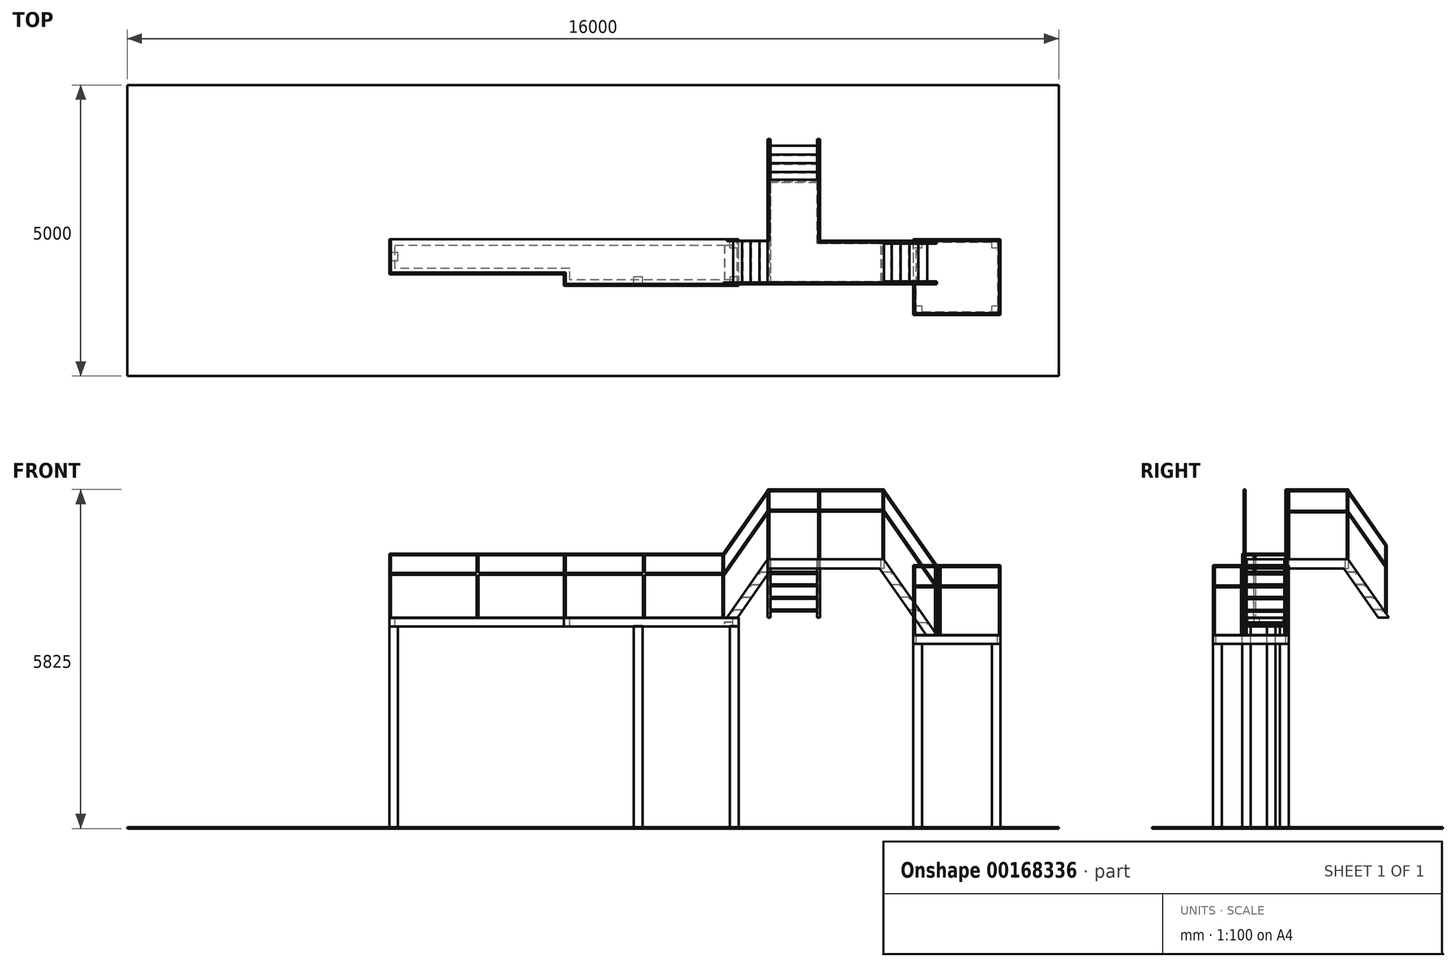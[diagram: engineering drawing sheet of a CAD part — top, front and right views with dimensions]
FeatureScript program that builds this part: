
annotation { "Feature Type Name" : "Feature", "Feature Type Description" : "" }
export const myFeature = defineFeature(function(context is Context, id is Id, definition is map)
    precondition{}
    {
        {
            var Q0;
            Q0=qCreatedBy(makeId("Top.planeOp"),FACE);
            var sketch = newSketch(context, id + "F0", { "sketchPlane" : qUnion([Q0])});
            skLineSegment(sketch, "E0.bottom", {"start": v(-500, 1500) * mm, "end": v(15500, 1500) * mm});
            skLineSegment(sketch, "E0.top", {"start": v(-500, -3500) * mm, "end": v(15500, -3500) * mm});
            skLineSegment(sketch, "E0.left", {"start": v(-500, 1500) * mm, "end": v(-500, -3500) * mm});
            skLineSegment(sketch, "E0.right", {"start": v(15500, 1500) * mm, "end": v(15500, -3500) * mm});
            skSolve(sketch);
        }
        {
            var Q0;
            Q0 = qSketchRegion(id + "F0", true);
            extrude(context, id + "F1", {"entities" : qUnion([Q0]), "oppositeDirection" : true, "depth" : 25 * mm});
        }
        {
            var Q0;
            Q0=qCreatedBy(makeId("Top.planeOp"),FACE);
            cPlane(context, id + "F2", {"entities" : qUnion([Q0]), "cplaneType" : CPlaneType.OFFSET, "offset" : 3600 * mm, "width" : 150 * mm, "height" : 150 * mm});
        }
        {
            var Q0;
            Q0=qCreatedBy(id+"F2.planeOp",FACE);
            var sketch = newSketch(context, id + "F3", { "sketchPlane" : qUnion([Q0])});
            skLineSegment(sketch, "E1", {"start": v(4000, -1150) * mm, "end": v(10000, -1150) * mm});
            skLineSegment(sketch, "E2", {"start": v(10000, -1950) * mm, "end": v(10000, -1150) * mm});
            skLineSegment(sketch, "E3", {"start": v(10000, -1950) * mm, "end": v(7000, -1950) * mm});
            skLineSegment(sketch, "E4", {"start": v(7000, -1950) * mm, "end": v(7000, -1750) * mm});
            skLineSegment(sketch, "E5", {"start": v(7000, -1750) * mm, "end": v(4000, -1750) * mm});
            skLineSegment(sketch, "E6", {"start": v(4000, -1750) * mm, "end": v(4000, -1150) * mm});
            skSolve(sketch);
        }
        {
            var Q0;
            Q0 = qSketchRegion(id + "F3", true);
            extrude(context, id + "F4", {"entities" : qUnion([Q0]), "oppositeDirection" : true, "depth" : 5 * mm});
        }
        {
            var Q0;
            Q0=makeQuery(id+"F4.opExtrude","SWEPT_FACE",FACE,{"disambiguationData":[OSD([sQuery(id+"F3.wireOp",EDGE,"E2")])]});
            var sketch = newSketch(context, id + "F5", { "sketchPlane" : qUnion([Q0])});
            skLineSegment(sketch, "E7.bottom", {"start": v(-1950, 3595) * mm, "end": v(-1850, 3595) * mm});
            skLineSegment(sketch, "E7.top", {"start": v(-1950, 3445) * mm, "end": v(-1850, 3445) * mm});
            skLineSegment(sketch, "E7.left", {"start": v(-1950, 3595) * mm, "end": v(-1950, 3445) * mm});
            skLineSegment(sketch, "E7.right", {"start": v(-1850, 3595) * mm, "end": v(-1850, 3445) * mm});
            skSolve(sketch);
        }
        {
            var Q0;
            Q0=qCreatedBy(id+"F2.planeOp",FACE);
            cPlane(context, id + "F6", {"entities" : qUnion([Q0]), "cplaneType" : CPlaneType.OFFSET, "offset" : 150 * mm, "oppositeDirection" : true, "width" : 150 * mm, "height" : 150 * mm});
        }
        {
            var Q0;
            Q0=qCreatedBy(id+"F6.planeOp",FACE);
            var sketch = newSketch(context, id + "F7", { "sketchPlane" : qUnion([Q0])});
            skLineSegment(sketch, "E8.0", {"start": v(10000, -1150) * mm, "end": v(10000, -1950) * mm});
            skLineSegment(sketch, "E9.0", {"start": v(10000, -1950) * mm, "end": v(7000, -1950) * mm});
            skLineSegment(sketch, "E10.0", {"start": v(7000, -1750) * mm, "end": v(4000, -1750) * mm});
            skLineSegment(sketch, "E11.0", {"start": v(7000, -1950) * mm, "end": v(7000, -1750) * mm});
            skLineSegment(sketch, "E12.0", {"start": v(4000, -1750) * mm, "end": v(4000, -1150) * mm});
            skLineSegment(sketch, "E13.0", {"start": v(4000, -1150) * mm, "end": v(10000, -1150) * mm});
            skPoint(sketch, "E14.0", {"position": v(10000, -1150) * mm});
            skSolve(sketch);
        }
        {
            var Q0;
            Q0=makeQuery(id+"F5.imprint","IMPRINT",FACE,{"disambiguationData":[TD([[makeQuery(id+"F5.imprint","IMPRINT",EDGE,{"derivedFrom":sQuery(id+"F5.wireOp",EDGE,"E7.bottom")}),-1.0]])]});
            var Q1;
            Q1 = qConstructionFilter(qBodyType(qCreatedBy(id + "F7" ,EDGE), BodyType.WIRE), ConstructionObject.NO);
            sweep(context, id + "F8", {"profiles" : qUnion([Q0]), "path" : qUnion([Q1])});
        }
        {
            var Q0;
            Q0=qCreatedBy(id+"F6.planeOp",FACE);
            var sketch = newSketch(context, id + "F9", { "sketchPlane" : qUnion([Q0])});
            skLineSegment(sketch, "E15.bottom", {"start": v(4000, -1375) * mm, "end": v(4150, -1375) * mm});
            skLineSegment(sketch, "E15.top", {"start": v(4000, -1525) * mm, "end": v(4150, -1525) * mm});
            skLineSegment(sketch, "E15.left", {"start": v(4000, -1375) * mm, "end": v(4000, -1525) * mm});
            skLineSegment(sketch, "E15.right", {"start": v(4150, -1375) * mm, "end": v(4150, -1525) * mm});
            skLineSegment(sketch, "E16.bottom", {"start": v(8200, -1800) * mm, "end": v(8350, -1800) * mm});
            skLineSegment(sketch, "E16.top", {"start": v(8200, -1950) * mm, "end": v(8350, -1950) * mm});
            skLineSegment(sketch, "E16.left", {"start": v(8200, -1800) * mm, "end": v(8200, -1950) * mm});
            skLineSegment(sketch, "E16.right", {"start": v(8350, -1800) * mm, "end": v(8350, -1950) * mm});
            skLineSegment(sketch, "E17.bottom", {"start": v(9850, -1150) * mm, "end": v(10000, -1150) * mm});
            skLineSegment(sketch, "E17.top", {"start": v(9850, -1300) * mm, "end": v(10000, -1300) * mm});
            skLineSegment(sketch, "E17.left", {"start": v(9850, -1150) * mm, "end": v(9850, -1300) * mm});
            skLineSegment(sketch, "E17.right", {"start": v(10000, -1150) * mm, "end": v(10000, -1300) * mm});
            skLineSegment(sketch, "E18.bottom", {"start": v(9850, -1950) * mm, "end": v(10000, -1950) * mm});
            skLineSegment(sketch, "E18.top", {"start": v(9850, -1800) * mm, "end": v(10000, -1800) * mm});
            skLineSegment(sketch, "E18.left", {"start": v(9850, -1950) * mm, "end": v(9850, -1800) * mm});
            skLineSegment(sketch, "E18.right", {"start": v(10000, -1950) * mm, "end": v(10000, -1800) * mm});
            skSolve(sketch);
        }
        {
            var Q0;
            Q0 = qSketchRegion(id + "F9", true);
            var Q1;
            Q1=makeQuery(id+"F1.opExtrude","CAP_FACE",FACE,{"disambiguationData":[OSD([sQuery(id+"F0.wireOp",EDGE,"E0.bottom"),sQuery(id+"F0.wireOp",EDGE,"E0.top"),sQuery(id+"F0.wireOp",EDGE,"E0.left"),sQuery(id+"F0.wireOp",EDGE,"E0.right")])],"isStart":true});
            extrude(context, id + "F10", {"entities" : qUnion([Q0]), "endBound" : BoundingType.UP_TO_SURFACE, "oppositeDirection" : true, "endBoundEntityFace" : qUnion([Q1]), "depth" : 25 * mm});
        }
        {
            var Q0;
            Q0=qCreatedBy(id+"F2.planeOp",FACE);
            cPlane(context, id + "F11", {"entities" : qUnion([Q0]), "cplaneType" : CPlaneType.OFFSET, "offset" : 300 * mm, "oppositeDirection" : true, "width" : 150 * mm, "height" : 150 * mm});
        }
        {
            var Q0;
            Q0=qCreatedBy(id+"F11.planeOp",FACE);
            var sketch = newSketch(context, id + "F12", { "sketchPlane" : qUnion([Q0])});
            skLineSegment(sketch, "E19.bottom", {"start": v(13000, -1150) * mm, "end": v(14500, -1150) * mm});
            skLineSegment(sketch, "E19.top", {"start": v(13000, -2450) * mm, "end": v(14500, -2450) * mm});
            skLineSegment(sketch, "E19.left", {"start": v(13000, -1150) * mm, "end": v(13000, -2450) * mm});
            skLineSegment(sketch, "E19.right", {"start": v(14500, -1150) * mm, "end": v(14500, -2450) * mm});
            skPoint(sketch, "E20.0", {"position": v(10000, -1150) * mm});
            skSolve(sketch);
        }
        {
            var Q0;
            Q0 = qSketchRegion(id + "F12", true);
            extrude(context, id + "F13", {"entities" : qUnion([Q0]), "oppositeDirection" : true, "depth" : 5 * mm});
        }
        {
            var Q0;
            Q0=qCreatedBy(id+"F11.planeOp",FACE);
            cPlane(context, id + "F14", {"entities" : qUnion([Q0]), "cplaneType" : CPlaneType.OFFSET, "offset" : 1300 * mm, "width" : 150 * mm, "height" : 150 * mm});
        }
        {
            var Q0;
            Q0=qCreatedBy(id+"F14.planeOp",FACE);
            var sketch = newSketch(context, id + "F15", { "sketchPlane" : qUnion([Q0])});
            skLineSegment(sketch, "E21.bottom", {"start": v(10500, -125) * mm, "end": v(11400, -125) * mm});
            skLineSegment(sketch, "E21.top", {"start": v(10500, -1925) * mm, "end": v(12500, -1925) * mm});
            skLineSegment(sketch, "E21.left", {"start": v(10500, -125) * mm, "end": v(10500, -1925) * mm});
            skLineSegment(sketch, "E21.right", {"start": v(11400, -125) * mm, "end": v(11400, -1175) * mm});
            skLineSegment(sketch, "E22", {"start": v(10950, -1777.45) * mm, "end": v(10950, -125) * mm, "construction": true});
            skLineSegment(sketch, "E23", {"start": v(12500, -1925) * mm, "end": v(12500, -1175) * mm});
            skLineSegment(sketch, "E24", {"start": v(12500, -1175) * mm, "end": v(11400, -1175) * mm});
            skSolve(sketch);
        }
        {
            var Q0;
            Q0 = qSketchRegion(id + "F15", true);
            extrude(context, id + "F16", {"entities" : qUnion([Q0]), "oppositeDirection" : true, "depth" : 5 * mm});
        }
        {
            var Q0;
            Q0=makeQuery(id+"F16.opExtrude","CAP_EDGE",EDGE,{"disambiguationData":[OSD([sQuery(id+"F15.wireOp",EDGE,"E23")])],"isStart":false});
            cPoint(context, id + "F17", {"entities" : qUnion([Q0]), "parameter" : 0.5});
        }
        {
            var Q0;
            Q0=makeQuery(id+"F16.opExtrude","SWEPT_FACE",FACE,{"disambiguationData":[OSD([sQuery(id+"F15.wireOp",EDGE,"E21.top")])]});
            var Q1;
            Q1 = qCreatedBy(id + "F17" ,VERTEX);
            cPlane(context, id + "F18", {"entities" : qUnion([Q0, Q1]), "cplaneType" : CPlaneType.PLANE_POINT, "offset" : 388 * mm, "oppositeDirection" : true, "width" : 150 * mm, "height" : 150 * mm});
        }
        {
            var Q0;
            Q0=qCreatedBy(id+"F18.planeOp",FACE);
            var sketch = newSketch(context, id + "F19", { "sketchPlane" : qUnion([Q0])});
            skLineSegment(sketch, "E25", {"start": v(10500, 4600) * mm, "end": v(10500, 4338.48) * mm});
            skLineSegment(sketch, "E26", {"start": v(10500, 4338.48) * mm, "end": v(9982.9, 3600) * mm});
            skLineSegment(sketch, "E27", {"start": v(9982.9, 3600) * mm, "end": v(9799.8, 3600) * mm});
            skLineSegment(sketch, "E28", {"start": v(9799.8, 3600) * mm, "end": v(10500, 4600) * mm});
            skSolve(sketch);
        }
        {
            var Q0;
            Q0 = qSketchRegion(id + "F19", true);
            extrude(context, id + "F20", {"entities" : qUnion([Q0]), "endBound" : BoundingType.SYMMETRIC, "depth" : 750 * mm});
        }
        {
            var Q0;
            Q0=makeQuery(id+"F20.opExtrude","SWEPT_FACE",FACE,{"disambiguationData":[OSD([sQuery(id+"F19.wireOp",EDGE,"E28")])]});
            var Q1;
            Q1=makeQuery(id+"F20.opExtrude","SWEPT_FACE",FACE,{"disambiguationData":[OSD([sQuery(id+"F19.wireOp",EDGE,"E25")])]});
            var Q2;
            Q2=makeQuery(id+"F20.opExtrude","SWEPT_FACE",FACE,{"disambiguationData":[OSD([sQuery(id+"F19.wireOp",EDGE,"E27")])]});
            shell(context, id + "F21", {"entities" : qUnion([Q0, Q1, Q2]), "thickness" : 3 * mm});
        }
        {
            var Q0;
            Q0=makeQuery(id+"F20.opExtrude","CAP_FACE",FACE,{"disambiguationData":[OSD([sQuery(id+"F19.wireOp",EDGE,"E25"),sQuery(id+"F19.wireOp",EDGE,"E26"),sQuery(id+"F19.wireOp",EDGE,"E27"),sQuery(id+"F19.wireOp",EDGE,"E28")])],"isStart":false});
            var sketch = newSketch(context, id + "F22", { "sketchPlane" : qUnion([Q0])});
            skLineSegment(sketch, "E29", {"start": v(10359.07, 4350) * mm, "end": v(10359.07, 4385) * mm});
            skLineSegment(sketch, "E30", {"start": v(10359.07, 4385) * mm, "end": v(10529.07, 4385) * mm});
            skLineSegment(sketch, "E31.0", {"start": v(10364.07, 4380) * mm, "end": v(10529.07, 4380) * mm});
            skLineSegment(sketch, "E31.1", {"start": v(10364.07, 4350) * mm, "end": v(10364.07, 4380) * mm});
            skLineSegment(sketch, "E32", {"start": v(10359.07, 4350) * mm, "end": v(10364.07, 4350) * mm});
            skLineSegment(sketch, "E33", {"start": v(10529.07, 4385) * mm, "end": v(10529.07, 4380) * mm});
            skLineSegment(sketch, "E34.1.0.0", {"start": v(10213.22, 4134.56) * mm, "end": v(10213.22, 4164.56) * mm});
            skLineSegment(sketch, "E34.1.0.1", {"start": v(10213.22, 4164.56) * mm, "end": v(10378.22, 4164.56) * mm});
            skLineSegment(sketch, "E34.1.0.2", {"start": v(10208.22, 4169.56) * mm, "end": v(10378.22, 4169.56) * mm});
            skLineSegment(sketch, "E34.1.0.3", {"start": v(10208.22, 4134.56) * mm, "end": v(10208.22, 4169.56) * mm});
            skLineSegment(sketch, "E34.1.0.4", {"start": v(10378.22, 4169.56) * mm, "end": v(10378.22, 4164.56) * mm});
            skLineSegment(sketch, "E34.1.0.5", {"start": v(10208.22, 4134.56) * mm, "end": v(10213.22, 4134.56) * mm});
            skLineSegment(sketch, "E34.2.0.0", {"start": v(10062.37, 3919.13) * mm, "end": v(10062.37, 3949.13) * mm});
            skLineSegment(sketch, "E34.2.0.1", {"start": v(10062.37, 3949.13) * mm, "end": v(10227.37, 3949.13) * mm});
            skLineSegment(sketch, "E34.2.0.2", {"start": v(10057.37, 3954.13) * mm, "end": v(10227.37, 3954.13) * mm});
            skLineSegment(sketch, "E34.2.0.3", {"start": v(10057.37, 3919.13) * mm, "end": v(10057.37, 3954.13) * mm});
            skLineSegment(sketch, "E34.2.0.4", {"start": v(10227.37, 3954.13) * mm, "end": v(10227.37, 3949.13) * mm});
            skLineSegment(sketch, "E34.2.0.5", {"start": v(10057.37, 3919.13) * mm, "end": v(10062.37, 3919.13) * mm});
            skLineSegment(sketch, "E34.direction1", {"start": v(10359.07, 4350) * mm, "end": v(10208.22, 4134.56) * mm, "construction": true});
            skLineSegment(sketch, "E35.0.3.0", {"start": v(9911.52, 3703.69) * mm, "end": v(9911.52, 3733.69) * mm});
            skLineSegment(sketch, "E35.3.3.0", {"start": v(9911.52, 3733.69) * mm, "end": v(10076.52, 3733.69) * mm});
            skLineSegment(sketch, "E35.6.3.0", {"start": v(9906.52, 3738.69) * mm, "end": v(10076.52, 3738.69) * mm});
            skLineSegment(sketch, "E35.9.3.0", {"start": v(9906.52, 3703.69) * mm, "end": v(9906.52, 3738.69) * mm});
            skLineSegment(sketch, "E35.12.3.0", {"start": v(10076.52, 3738.69) * mm, "end": v(10076.52, 3733.69) * mm});
            skLineSegment(sketch, "E35.15.3.0", {"start": v(9906.52, 3703.69) * mm, "end": v(9911.52, 3703.69) * mm});
            skLineSegment(sketch, "E35.0.4.0", {"start": v(9760.67, 3488.25) * mm, "end": v(9760.67, 3518.25) * mm});
            skLineSegment(sketch, "E35.3.4.0", {"start": v(9760.67, 3518.25) * mm, "end": v(9925.67, 3518.25) * mm});
            skLineSegment(sketch, "E35.6.4.0", {"start": v(9755.67, 3523.25) * mm, "end": v(9925.67, 3523.25) * mm});
            skLineSegment(sketch, "E35.9.4.0", {"start": v(9755.67, 3488.25) * mm, "end": v(9755.67, 3523.25) * mm});
            skLineSegment(sketch, "E35.12.4.0", {"start": v(9925.67, 3523.25) * mm, "end": v(9925.67, 3518.25) * mm});
            skLineSegment(sketch, "E35.15.4.0", {"start": v(9755.67, 3488.25) * mm, "end": v(9760.67, 3488.25) * mm});
            skSolve(sketch);
        }
        {
            var Q0;
            Q0 = qSketchRegion(id + "F22", true);
            var Q1;
            Q1=makeQuery(id+"F20.opExtrude","CAP_FACE",FACE,{"disambiguationData":[OSD([sQuery(id+"F19.wireOp",EDGE,"E25"),sQuery(id+"F19.wireOp",EDGE,"E26"),sQuery(id+"F19.wireOp",EDGE,"E27"),sQuery(id+"F19.wireOp",EDGE,"E28")])],"isStart":true});
            extrude(context, id + "F23", {"entities" : qUnion([Q0]), "operationType" : NewBodyOperationType.ADD, "endBound" : BoundingType.UP_TO_SURFACE, "oppositeDirection" : true, "endBoundEntityFace" : qUnion([Q1]), "depth" : 25 * mm});
        }
        {
            var Q0;
            Q0=makeQuery(id+"F16.opExtrude","CAP_EDGE",EDGE,{"disambiguationData":[OSD([sQuery(id+"F15.wireOp",EDGE,"E21.bottom")])],"isStart":true});
            cPoint(context, id + "F24", {"entities" : qUnion([Q0]), "parameter" : 0.5});
        }
        {
            var Q0;
            Q0=makeQuery(id+"F16.opExtrude","SWEPT_FACE",FACE,{"disambiguationData":[OSD([sQuery(id+"F15.wireOp",EDGE,"E21.left")])]});
            var Q1;
            Q1 = qCreatedBy(id + "F24" ,VERTEX);
            cPlane(context, id + "F25", {"entities" : qUnion([Q0, Q1]), "cplaneType" : CPlaneType.PLANE_POINT, "offset" : 25 * mm, "width" : 150 * mm, "height" : 150 * mm});
        }
        {
            var Q0;
            Q0=makeQuery(id+"F16.opExtrude","CAP_FACE",FACE,{"disambiguationData":[OSD([sQuery(id+"F15.wireOp",EDGE,"E21.bottom"),sQuery(id+"F15.wireOp",EDGE,"E21.top"),sQuery(id+"F15.wireOp",EDGE,"E21.left"),sQuery(id+"F15.wireOp",EDGE,"E21.right")])],"isStart":false});
            var sketch = newSketch(context, id + "F26", { "sketchPlane" : qUnion([Q0])});
            skLineSegment(sketch, "E36.0.0", {"start": v(10500, 125) * mm, "end": v(11400, 125) * mm});
            skLineSegment(sketch, "E36.0.1", {"start": v(11400, 125) * mm, "end": v(11400, 125) * mm});
            skLineSegment(sketch, "E36.0.2", {"start": v(10530, 1925) * mm, "end": v(10500, 1925) * mm});
            skLineSegment(sketch, "E36.0.3", {"start": v(10500, 1925) * mm, "end": v(10500, 125) * mm});
            skLineSegment(sketch, "E37.0", {"start": v(-505, -1505) * mm, "end": v(15505, -1505) * mm});
            skLineSegment(sketch, "E37.1", {"start": v(-505, 3505) * mm, "end": v(-505, -1505) * mm});
            skLineSegment(sketch, "E37.2", {"start": v(15505, 3505) * mm, "end": v(-505, 3505) * mm});
            skLineSegment(sketch, "E37.3", {"start": v(15505, -1505) * mm, "end": v(15505, 3505) * mm});
            skLineSegment(sketch, "E38.0", {"start": v(11350, 1225) * mm, "end": v(11350, 175) * mm});
            skLineSegment(sketch, "E38.1", {"start": v(10550, 175) * mm, "end": v(10550, 1875) * mm});
            skLineSegment(sketch, "E38.2", {"start": v(10550, 1875) * mm, "end": v(12450, 1875) * mm});
            skLineSegment(sketch, "E38.3", {"start": v(11350, 175) * mm, "end": v(10550, 175) * mm});
            skLineSegment(sketch, "E38.4", {"start": v(12450, 1875) * mm, "end": v(12450, 1225) * mm});
            skLineSegment(sketch, "E38.5", {"start": v(12450, 1225) * mm, "end": v(11350, 1225) * mm});
            skSolve(sketch);
        }
        {
            var Q0;
            Q0=makeQuery(id+"F26.imprint","IMPRINT",FACE,{"disambiguationData":[TD([[makeQuery(id+"F26.imprint","IMPRINT",EDGE,{"derivedFrom":sQuery(id+"F26.wireOp",EDGE,"E36.0.0")}),1.0]])]});
            extrude(context, id + "F27", {"entities" : qUnion([Q0]), "depth" : 150 * mm});
        }
        {
            var Q0;
            Q0=makeQuery(id+"F27.opExtrude","SWEPT_FACE",FACE,{"disambiguationData":[OSD([sQuery(id+"F15.wireOp",EDGE,"E21.right")])]});
            var sketch = newSketch(context, id + "F28", { "sketchPlane" : qUnion([Q0])});
            skLineSegment(sketch, "E39", {"start": v(-125, 4595) * mm, "end": v(-203.09, 4445) * mm});
            skLineSegment(sketch, "E40", {"start": v(387.9, 3601) * mm, "end": v(-203.09, 4445) * mm});
            skLineSegment(sketch, "E41", {"start": v(-125, 4595) * mm, "end": v(571, 3601) * mm});
            skLineSegment(sketch, "E42", {"start": v(571, 3601) * mm, "end": v(387.9, 3601) * mm});
            skSolve(sketch);
        }
        {
            var Q0;
            Q0 = qSketchRegion(id + "F28", true);
            extrude(context, id + "F29", {"entities" : qUnion([Q0]), "oppositeDirection" : true, "depth" : 50 * mm});
        }
        {
            var Q0;
            Q0=makeQuery(id+"F29.opExtrude","SWEPT_BODY",BODY,{"disambiguationData":[OSD([sQuery(id+"F28.wireOp",EDGE,"E39"),sQuery(id+"F28.wireOp",EDGE,"E40"),sQuery(id+"F28.wireOp",EDGE,"yFBp22pC-zta5-zhW2-1WAF-goKuTXkOEWaN"),sQuery(id+"F28.wireOp",EDGE,"E41")])]});
            var Q1;
            Q1=qCreatedBy(id+"F25.planeOp",FACE);
            mirror(context, id + "F30", {"operationType" : NewBodyOperationType.ADD, "entities" : qUnion([Q0]), "mirrorPlane" : qUnion([Q1])});
        }
        {
            var Q0;
            Q0=makeQuery(id+"F30.boolean.opBoolean","MERGE",FACE,{"derivedFrom":[makeQuery(id+"F27.opExtrude","SWEPT_FACE",FACE,{"disambiguationData":[OSD([sQuery(id+"F26.wireOp",EDGE,"4b7b3fe2-faf2-46bd-95d1-659c540ad528.3")])]}),makeQuery(id+"F29.opExtrude","CAP_FACE",FACE,{"disambiguationData":[OSD([sQuery(id+"F28.wireOp",EDGE,"E39"),sQuery(id+"F28.wireOp",EDGE,"E40"),sQuery(id+"F28.wireOp",EDGE,"yFBp22pC-zta5-zhW2-1WAF-goKuTXkOEWaN"),sQuery(id+"F28.wireOp",EDGE,"E41")])],"isStart":false})]});
            var sketch = newSketch(context, id + "F31", { "sketchPlane" : qUnion([Q0])});
            skLineSegment(sketch, "E43", {"start": v(-7.43, 4385) * mm, "end": v(157.57, 4385) * mm});
            skLineSegment(sketch, "E44", {"start": v(157.57, 4385) * mm, "end": v(157.57, 4380) * mm});
            skLineSegment(sketch, "E45", {"start": v(157.57, 4380) * mm, "end": v(-2.43, 4380) * mm});
            skLineSegment(sketch, "E46", {"start": v(-2.43, 4380) * mm, "end": v(-2.43, 4350) * mm});
            skLineSegment(sketch, "E47", {"start": v(-2.43, 4350) * mm, "end": v(-7.43, 4350) * mm});
            skLineSegment(sketch, "E48", {"start": v(-7.43, 4350) * mm, "end": v(-7.43, 4385) * mm});
            skLineSegment(sketch, "E49.1.0.0", {"start": v(-157.7, 4170.38) * mm, "end": v(7.3, 4170.38) * mm});
            skLineSegment(sketch, "E49.1.0.1", {"start": v(7.3, 4165.38) * mm, "end": v(-152.7, 4165.38) * mm});
            skLineSegment(sketch, "E49.1.0.2", {"start": v(-152.7, 4135.38) * mm, "end": v(-157.7, 4135.38) * mm});
            skLineSegment(sketch, "E49.1.0.3", {"start": v(-157.7, 4135.38) * mm, "end": v(-157.7, 4170.38) * mm});
            skLineSegment(sketch, "E49.1.0.4", {"start": v(-152.7, 4165.38) * mm, "end": v(-152.7, 4135.38) * mm});
            skLineSegment(sketch, "E49.1.0.5", {"start": v(7.3, 4170.38) * mm, "end": v(7.3, 4165.38) * mm});
            skLineSegment(sketch, "E49.2.0.0", {"start": v(-307.98, 3955.76) * mm, "end": v(-142.98, 3955.76) * mm});
            skLineSegment(sketch, "E49.2.0.1", {"start": v(-142.98, 3950.76) * mm, "end": v(-302.98, 3950.76) * mm});
            skLineSegment(sketch, "E49.2.0.2", {"start": v(-302.98, 3920.76) * mm, "end": v(-307.98, 3920.76) * mm});
            skLineSegment(sketch, "E49.2.0.3", {"start": v(-307.98, 3920.76) * mm, "end": v(-307.98, 3955.76) * mm});
            skLineSegment(sketch, "E49.2.0.4", {"start": v(-302.98, 3950.76) * mm, "end": v(-302.98, 3920.76) * mm});
            skLineSegment(sketch, "E49.2.0.5", {"start": v(-142.98, 3955.76) * mm, "end": v(-142.98, 3950.76) * mm});
            skLineSegment(sketch, "E49.direction1", {"start": v(-7.43, 4350) * mm, "end": v(-157.7, 4135.38) * mm, "construction": true});
            skLineSegment(sketch, "E50.0.3.0", {"start": v(-458.26, 3741.15) * mm, "end": v(-293.26, 3741.15) * mm});
            skLineSegment(sketch, "E50.3.3.0", {"start": v(-293.26, 3736.15) * mm, "end": v(-453.26, 3736.15) * mm});
            skLineSegment(sketch, "E50.6.3.0", {"start": v(-453.26, 3706.15) * mm, "end": v(-458.26, 3706.15) * mm});
            skLineSegment(sketch, "E50.9.3.0", {"start": v(-458.26, 3706.15) * mm, "end": v(-458.26, 3741.15) * mm});
            skLineSegment(sketch, "E50.12.3.0", {"start": v(-453.26, 3736.15) * mm, "end": v(-453.26, 3706.15) * mm});
            skLineSegment(sketch, "E50.15.3.0", {"start": v(-293.26, 3741.15) * mm, "end": v(-293.26, 3736.15) * mm});
            skSolve(sketch);
        }
        {
            var Q0;
            Q0 = qSketchRegion(id + "F31", true);
            var Q1;
            Q1=makeQuery(id+"F30.boolean.opBoolean","MERGE",FACE,{"derivedFrom":[makeQuery(id+"F27.opExtrude","SWEPT_FACE",FACE,{"disambiguationData":[OSD([sQuery(id+"F26.wireOp",EDGE,"E38.1")])]}),makeQuery(id+"F30.opPattern","COPY",FACE,{"derivedFrom":makeQuery(id+"F29.opExtrude","CAP_FACE",FACE,{"disambiguationData":[OSD([sQuery(id+"F28.wireOp",EDGE,"E39"),sQuery(id+"F28.wireOp",EDGE,"E40"),sQuery(id+"F28.wireOp",EDGE,"E41"),sQuery(id+"F28.wireOp",EDGE,"E42")])],"isStart":false}),"instanceName":"1"})]});
            extrude(context, id + "F32", {"entities" : qUnion([Q0]), "operationType" : NewBodyOperationType.ADD, "endBound" : BoundingType.UP_TO_SURFACE, "endBoundEntityFace" : qUnion([Q1]), "depth" : 413 * mm});
        }
        {
            var Q0;
            Q0=qCreatedBy(id+"F18.planeOp",FACE);
            var sketch = newSketch(context, id + "F33", { "sketchPlane" : qUnion([Q0])});
            skLineSegment(sketch, "E51", {"start": v(12500, 4595) * mm, "end": v(12421.91, 4445) * mm});
            skLineSegment(sketch, "E52", {"start": v(12421.91, 4445) * mm, "end": v(13223.65, 3300) * mm});
            skLineSegment(sketch, "E53", {"start": v(13223.65, 3300) * mm, "end": v(13406.77, 3300) * mm});
            skLineSegment(sketch, "E54", {"start": v(13406.77, 3300) * mm, "end": v(12500, 4595) * mm});
            skSolve(sketch);
        }
        {
            var Q0;
            Q0 = qSketchRegion(id + "F33", true);
            extrude(context, id + "F34", {"entities" : qUnion([Q0]), "depth" : 375 * mm, "hasSecondDirection" : true, "secondDirectionOppositeDirection" : false, "secondDirectionDepth" : 325 * mm});
        }
        {
            var Q0;
            Q0=makeQuery(id+"F34.opExtrude","SWEPT_BODY",BODY,{"disambiguationData":[OSD([sQuery(id+"F33.wireOp",EDGE,"E51"),sQuery(id+"F33.wireOp",EDGE,"E52"),sQuery(id+"F33.wireOp",EDGE,"E53"),sQuery(id+"F33.wireOp",EDGE,"E54")])]});
            var Q1;
            Q1=qCreatedBy(id+"F18.planeOp",FACE);
            mirror(context, id + "F35", {"operationType" : NewBodyOperationType.ADD, "entities" : qUnion([Q0]), "mirrorPlane" : qUnion([Q1])});
        }
        {
            var Q0;
            Q0=qCreatedBy(id+"F18.planeOp",FACE);
            var sketch = newSketch(context, id + "F36", { "sketchPlane" : qUnion([Q0])});
            skLineSegment(sketch, "E55", {"start": v(12467.43, 4385) * mm, "end": v(12632.43, 4385) * mm});
            skLineSegment(sketch, "E56", {"start": v(12467.43, 4385) * mm, "end": v(12467.43, 4380) * mm});
            skLineSegment(sketch, "E57", {"start": v(12627.43, 4380) * mm, "end": v(12467.43, 4380) * mm});
            skLineSegment(sketch, "E58", {"start": v(12627.43, 4380) * mm, "end": v(12627.43, 4350) * mm});
            skLineSegment(sketch, "E59", {"start": v(12632.43, 4350) * mm, "end": v(12627.43, 4350) * mm});
            skLineSegment(sketch, "E60", {"start": v(12632.43, 4350) * mm, "end": v(12632.43, 4385) * mm});
            skLineSegment(sketch, "E61.1.0.0", {"start": v(12784.43, 4132.92) * mm, "end": v(12784.43, 4167.92) * mm});
            skLineSegment(sketch, "E61.1.0.1", {"start": v(12619.43, 4167.92) * mm, "end": v(12784.43, 4167.92) * mm});
            skLineSegment(sketch, "E61.1.0.2", {"start": v(12779.43, 4162.92) * mm, "end": v(12619.43, 4162.92) * mm});
            skLineSegment(sketch, "E61.1.0.3", {"start": v(12779.43, 4162.92) * mm, "end": v(12779.43, 4132.92) * mm});
            skLineSegment(sketch, "E61.1.0.4", {"start": v(12784.43, 4132.92) * mm, "end": v(12779.43, 4132.92) * mm});
            skLineSegment(sketch, "E61.1.0.5", {"start": v(12619.43, 4167.92) * mm, "end": v(12619.43, 4162.92) * mm});
            skLineSegment(sketch, "E61.2.0.0", {"start": v(12936.42, 3915.85) * mm, "end": v(12936.42, 3950.85) * mm});
            skLineSegment(sketch, "E61.2.0.1", {"start": v(12771.42, 3950.85) * mm, "end": v(12936.42, 3950.85) * mm});
            skLineSegment(sketch, "E61.2.0.2", {"start": v(12931.42, 3945.85) * mm, "end": v(12771.42, 3945.85) * mm});
            skLineSegment(sketch, "E61.2.0.3", {"start": v(12931.42, 3945.85) * mm, "end": v(12931.42, 3915.85) * mm});
            skLineSegment(sketch, "E61.2.0.4", {"start": v(12936.42, 3915.85) * mm, "end": v(12931.42, 3915.85) * mm});
            skLineSegment(sketch, "E61.2.0.5", {"start": v(12771.42, 3950.85) * mm, "end": v(12771.42, 3945.85) * mm});
            skLineSegment(sketch, "E61.direction1", {"start": v(12467.43, 4380) * mm, "end": v(12619.43, 4162.92) * mm, "construction": true});
            skLineSegment(sketch, "E62.0.3.0", {"start": v(13088.42, 3698.77) * mm, "end": v(13088.42, 3733.77) * mm});
            skLineSegment(sketch, "E62.3.3.0", {"start": v(12923.42, 3733.77) * mm, "end": v(13088.42, 3733.77) * mm});
            skLineSegment(sketch, "E62.6.3.0", {"start": v(13083.42, 3728.77) * mm, "end": v(12923.42, 3728.77) * mm});
            skLineSegment(sketch, "E62.9.3.0", {"start": v(13083.42, 3728.77) * mm, "end": v(13083.42, 3698.77) * mm});
            skLineSegment(sketch, "E62.12.3.0", {"start": v(13088.42, 3698.77) * mm, "end": v(13083.42, 3698.77) * mm});
            skLineSegment(sketch, "E62.15.3.0", {"start": v(12923.42, 3733.77) * mm, "end": v(12923.42, 3728.77) * mm});
            skLineSegment(sketch, "E62.0.4.0", {"start": v(13240.42, 3481.7) * mm, "end": v(13240.42, 3516.7) * mm});
            skLineSegment(sketch, "E62.3.4.0", {"start": v(13075.42, 3516.7) * mm, "end": v(13240.42, 3516.7) * mm});
            skLineSegment(sketch, "E62.6.4.0", {"start": v(13235.42, 3511.7) * mm, "end": v(13075.42, 3511.7) * mm});
            skLineSegment(sketch, "E62.9.4.0", {"start": v(13235.42, 3511.7) * mm, "end": v(13235.42, 3481.7) * mm});
            skLineSegment(sketch, "E62.12.4.0", {"start": v(13240.42, 3481.7) * mm, "end": v(13235.42, 3481.7) * mm});
            skLineSegment(sketch, "E62.15.4.0", {"start": v(13075.42, 3516.7) * mm, "end": v(13075.42, 3511.7) * mm});
            skSolve(sketch);
        }
        {
            var Q0;
            Q0 = qSketchRegion(id + "F36", true);
            extrude(context, id + "F37", {"entities" : qUnion([Q0]), "operationType" : NewBodyOperationType.ADD, "endBound" : BoundingType.SYMMETRIC, "depth" : 650 * mm});
        }
        {
            var Q0;
            Q0=makeQuery(id+"F13.opExtrude","CAP_FACE",FACE,{"disambiguationData":[OSD([sQuery(id+"F12.wireOp",EDGE,"E19.bottom"),sQuery(id+"F12.wireOp",EDGE,"E19.top"),sQuery(id+"F12.wireOp",EDGE,"E19.left"),sQuery(id+"F12.wireOp",EDGE,"E19.right")])],"isStart":false});
            var sketch = newSketch(context, id + "F38", { "sketchPlane" : qUnion([Q0])});
            skLineSegment(sketch, "E63.0", {"start": v(13050, 1200) * mm, "end": v(14450, 1200) * mm});
            skLineSegment(sketch, "E63.1", {"start": v(13050, 2400) * mm, "end": v(13050, 1200) * mm});
            skLineSegment(sketch, "E63.2", {"start": v(14450, 2400) * mm, "end": v(13050, 2400) * mm});
            skLineSegment(sketch, "E63.3", {"start": v(14450, 1200) * mm, "end": v(14450, 2400) * mm});
            skSolve(sketch);
        }
        {
            var Q0;
            Q0=makeQuery(id+"F38.imprint","IMPRINT",FACE,{"disambiguationData":[TD([[makeQuery(id+"F38.imprint","IMPRINT",EDGE,{"derivedFrom":sQuery(id+"F38.wireOp",EDGE,"E63.0")}),-1.0]])]});
            extrude(context, id + "F39", {"entities" : qUnion([Q0]), "depth" : 150 * mm});
        }
        {
            var Q0;
            Q0=makeQuery(id+"F39.opExtrude","CAP_FACE",FACE,{"disambiguationData":[OSD([sQuery(id+"F12.wireOp",EDGE,"E19.bottom"),sQuery(id+"F12.wireOp",EDGE,"E19.top"),sQuery(id+"F12.wireOp",EDGE,"E19.left"),sQuery(id+"F12.wireOp",EDGE,"E19.right"),sQuery(id+"F38.wireOp",EDGE,"E63.0"),sQuery(id+"F38.wireOp",EDGE,"E63.1"),sQuery(id+"F38.wireOp",EDGE,"E63.2"),sQuery(id+"F38.wireOp",EDGE,"E63.3")])],"isStart":false});
            var sketch = newSketch(context, id + "F40", { "sketchPlane" : qUnion([Q0])});
            skLineSegment(sketch, "E64.bottom", {"start": v(14350, 1150) * mm, "end": v(14500, 1150) * mm});
            skLineSegment(sketch, "E64.top", {"start": v(14350, 1300) * mm, "end": v(14500, 1300) * mm});
            skLineSegment(sketch, "E64.left", {"start": v(14350, 1150) * mm, "end": v(14350, 1300) * mm});
            skLineSegment(sketch, "E64.right", {"start": v(14500, 1150) * mm, "end": v(14500, 1300) * mm});
            skLineSegment(sketch, "E65.bottom", {"start": v(13000, 2300) * mm, "end": v(13150, 2300) * mm});
            skLineSegment(sketch, "E65.top", {"start": v(13000, 2450) * mm, "end": v(13150, 2450) * mm});
            skLineSegment(sketch, "E65.left", {"start": v(13000, 2300) * mm, "end": v(13000, 2450) * mm});
            skLineSegment(sketch, "E65.right", {"start": v(13150, 2300) * mm, "end": v(13150, 2450) * mm});
            skLineSegment(sketch, "E66.bottom", {"start": v(13000, 1150) * mm, "end": v(13150, 1150) * mm});
            skLineSegment(sketch, "E66.top", {"start": v(13000, 1300) * mm, "end": v(13150, 1300) * mm});
            skLineSegment(sketch, "E66.left", {"start": v(13000, 1150) * mm, "end": v(13000, 1300) * mm});
            skLineSegment(sketch, "E66.right", {"start": v(13150, 1150) * mm, "end": v(13150, 1300) * mm});
            skLineSegment(sketch, "E67.bottom", {"start": v(14350, 2300) * mm, "end": v(14500, 2300) * mm});
            skLineSegment(sketch, "E67.top", {"start": v(14350, 2450) * mm, "end": v(14500, 2450) * mm});
            skLineSegment(sketch, "E67.left", {"start": v(14350, 2300) * mm, "end": v(14350, 2450) * mm});
            skLineSegment(sketch, "E67.right", {"start": v(14500, 2300) * mm, "end": v(14500, 2450) * mm});
            skSolve(sketch);
        }
        {
            var Q0;
            Q0 = qSketchRegion(id + "F40", true);
            var Q1;
            Q1=makeQuery(id+"F1.opExtrude","CAP_FACE",FACE,{"disambiguationData":[OSD([sQuery(id+"F0.wireOp",EDGE,"E0.bottom"),sQuery(id+"F0.wireOp",EDGE,"E0.top"),sQuery(id+"F0.wireOp",EDGE,"E0.left"),sQuery(id+"F0.wireOp",EDGE,"E0.right")])],"isStart":true});
            extrude(context, id + "F41", {"entities" : qUnion([Q0]), "endBound" : BoundingType.UP_TO_SURFACE, "endBoundEntityFace" : qUnion([Q1]), "depth" : 25 * mm});
        }
        {
            var Q0;
            Q0=makeQuery(id+"F4.opExtrude","CAP_FACE",FACE,{"disambiguationData":[OSD([sQuery(id+"F3.wireOp",EDGE,"E1"),sQuery(id+"F3.wireOp",EDGE,"E2"),sQuery(id+"F3.wireOp",EDGE,"E3"),sQuery(id+"F3.wireOp",EDGE,"E4"),sQuery(id+"F3.wireOp",EDGE,"E5"),sQuery(id+"F3.wireOp",EDGE,"E6")])],"isStart":true});
            var sketch = newSketch(context, id + "F42", { "sketchPlane" : qUnion([Q0])});
            skLineSegment(sketch, "E68.bottom", {"start": v(4000, -1150) * mm, "end": v(4030, -1150) * mm});
            skLineSegment(sketch, "E68.top", {"start": v(4000, -1180) * mm, "end": v(4030, -1180) * mm});
            skLineSegment(sketch, "E68.left", {"start": v(4000, -1150) * mm, "end": v(4000, -1180) * mm});
            skLineSegment(sketch, "E68.right", {"start": v(4030, -1150) * mm, "end": v(4030, -1180) * mm});
            skLineSegment(sketch, "E69.bottom", {"start": v(4000, -1750) * mm, "end": v(4030, -1750) * mm});
            skLineSegment(sketch, "E69.top", {"start": v(4000, -1720) * mm, "end": v(4030, -1720) * mm});
            skLineSegment(sketch, "E69.left", {"start": v(4000, -1750) * mm, "end": v(4000, -1720) * mm});
            skLineSegment(sketch, "E69.right", {"start": v(4030, -1750) * mm, "end": v(4030, -1720) * mm});
            skLineSegment(sketch, "E70.1.0.0", {"start": v(5500, -1750) * mm, "end": v(5500, -1720) * mm});
            skLineSegment(sketch, "E70.1.0.1", {"start": v(5500, -1720) * mm, "end": v(5530, -1720) * mm});
            skLineSegment(sketch, "E70.1.0.2", {"start": v(5530, -1750) * mm, "end": v(5530, -1720) * mm});
            skLineSegment(sketch, "E70.1.0.3", {"start": v(5500, -1750) * mm, "end": v(5530, -1750) * mm});
            skLineSegment(sketch, "E70.2.0.0", {"start": v(7000, -1750) * mm, "end": v(7000, -1720) * mm});
            skLineSegment(sketch, "E70.2.0.1", {"start": v(7000, -1720) * mm, "end": v(7030, -1720) * mm});
            skLineSegment(sketch, "E70.2.0.2", {"start": v(7030, -1750) * mm, "end": v(7030, -1720) * mm});
            skLineSegment(sketch, "E70.2.0.3", {"start": v(7000, -1750) * mm, "end": v(7030, -1750) * mm});
            skLineSegment(sketch, "E70.direction1", {"start": v(4000, -1750) * mm, "end": v(5500, -1750) * mm, "construction": true});
            skLineSegment(sketch, "E71.bottom", {"start": v(7000, -1920) * mm, "end": v(7030, -1920) * mm});
            skLineSegment(sketch, "E71.top", {"start": v(7000, -1950) * mm, "end": v(7030, -1950) * mm});
            skLineSegment(sketch, "E71.left", {"start": v(7000, -1920) * mm, "end": v(7000, -1950) * mm});
            skLineSegment(sketch, "E71.right", {"start": v(7030, -1920) * mm, "end": v(7030, -1950) * mm});
            skLineSegment(sketch, "E72.1.0.0", {"start": v(8360, -1950) * mm, "end": v(8390, -1950) * mm});
            skLineSegment(sketch, "E72.1.0.1", {"start": v(8390, -1920) * mm, "end": v(8390, -1950) * mm});
            skLineSegment(sketch, "E72.1.0.2", {"start": v(8360, -1920) * mm, "end": v(8390, -1920) * mm});
            skLineSegment(sketch, "E72.1.0.3", {"start": v(8360, -1920) * mm, "end": v(8360, -1950) * mm});
            skLineSegment(sketch, "E72.2.0.0", {"start": v(9720, -1950) * mm, "end": v(9750, -1950) * mm});
            skLineSegment(sketch, "E72.2.0.1", {"start": v(9750, -1920) * mm, "end": v(9750, -1950) * mm});
            skLineSegment(sketch, "E72.2.0.2", {"start": v(9720, -1920) * mm, "end": v(9750, -1920) * mm});
            skLineSegment(sketch, "E72.2.0.3", {"start": v(9720, -1920) * mm, "end": v(9720, -1950) * mm});
            skLineSegment(sketch, "E72.direction1", {"start": v(7000, -1950) * mm, "end": v(8360, -1950) * mm, "construction": true});
            skSolve(sketch);
        }
        {
            var Q0;
            Q0 = qSketchRegion(id + "F42", true);
            extrude(context, id + "F43", {"entities" : qUnion([Q0]), "operationType" : NewBodyOperationType.ADD, "depth" : 1100 * mm});
        }
        {
            var Q0;
            Q0=makeQuery(id+"F16.opExtrude","CAP_FACE",FACE,{"disambiguationData":[OSD([sQuery(id+"F15.wireOp",EDGE,"E21.bottom"),sQuery(id+"F15.wireOp",EDGE,"E21.top"),sQuery(id+"F15.wireOp",EDGE,"E21.left"),sQuery(id+"F15.wireOp",EDGE,"E21.right"),sQuery(id+"F15.wireOp",EDGE,"E23"),sQuery(id+"F15.wireOp",EDGE,"E24")])],"isStart":true});
            var sketch = newSketch(context, id + "F44", { "sketchPlane" : qUnion([Q0])});
            skLineSegment(sketch, "E73.bottom", {"start": v(10500, -1895) * mm, "end": v(10530, -1895) * mm});
            skLineSegment(sketch, "E73.top", {"start": v(10500, -1925) * mm, "end": v(10530, -1925) * mm});
            skLineSegment(sketch, "E73.left", {"start": v(10500, -1895) * mm, "end": v(10500, -1925) * mm});
            skLineSegment(sketch, "E73.right", {"start": v(10530, -1895) * mm, "end": v(10530, -1925) * mm});
            skLineSegment(sketch, "E74.bottom", {"start": v(10500, -125) * mm, "end": v(10530, -125) * mm});
            skLineSegment(sketch, "E74.top", {"start": v(10500, -155) * mm, "end": v(10530, -155) * mm});
            skLineSegment(sketch, "E74.left", {"start": v(10500, -125) * mm, "end": v(10500, -155) * mm});
            skLineSegment(sketch, "E74.right", {"start": v(10530, -125) * mm, "end": v(10530, -155) * mm});
            skLineSegment(sketch, "E75.bottom", {"start": v(11370, -1175) * mm, "end": v(11400, -1175) * mm});
            skLineSegment(sketch, "E75.top", {"start": v(11370, -1205) * mm, "end": v(11400, -1205) * mm});
            skLineSegment(sketch, "E75.left", {"start": v(11370, -1175) * mm, "end": v(11370, -1205) * mm});
            skLineSegment(sketch, "E75.right", {"start": v(11400, -1175) * mm, "end": v(11400, -1205) * mm});
            skLineSegment(sketch, "E76.bottom", {"start": v(11370, -125) * mm, "end": v(11400, -125) * mm});
            skLineSegment(sketch, "E76.top", {"start": v(11370, -155) * mm, "end": v(11400, -155) * mm});
            skLineSegment(sketch, "E76.left", {"start": v(11370, -125) * mm, "end": v(11370, -155) * mm});
            skLineSegment(sketch, "E76.right", {"start": v(11400, -125) * mm, "end": v(11400, -155) * mm});
            skLineSegment(sketch, "E77.bottom", {"start": v(12470, -1895) * mm, "end": v(12500, -1895) * mm});
            skLineSegment(sketch, "E77.top", {"start": v(12470, -1925) * mm, "end": v(12500, -1925) * mm});
            skLineSegment(sketch, "E77.left", {"start": v(12470, -1895) * mm, "end": v(12470, -1925) * mm});
            skLineSegment(sketch, "E77.right", {"start": v(12500, -1895) * mm, "end": v(12500, -1925) * mm});
            skLineSegment(sketch, "E78.bottom", {"start": v(12470, -1175) * mm, "end": v(12500, -1175) * mm});
            skLineSegment(sketch, "E78.top", {"start": v(12470, -1205) * mm, "end": v(12500, -1205) * mm});
            skLineSegment(sketch, "E78.left", {"start": v(12470, -1175) * mm, "end": v(12470, -1205) * mm});
            skLineSegment(sketch, "E78.right", {"start": v(12500, -1175) * mm, "end": v(12500, -1205) * mm});
            skLineSegment(sketch, "E79.bottom", {"start": v(10500, -1145) * mm, "end": v(10530, -1145) * mm});
            skLineSegment(sketch, "E79.top", {"start": v(10500, -1175) * mm, "end": v(10530, -1175) * mm});
            skLineSegment(sketch, "E79.left", {"start": v(10500, -1145) * mm, "end": v(10500, -1175) * mm});
            skLineSegment(sketch, "E79.right", {"start": v(10530, -1145) * mm, "end": v(10530, -1175) * mm});
            skSolve(sketch);
        }
        {
            var Q0;
            Q0 = qSketchRegion(id + "F44", true);
            extrude(context, id + "F45", {"entities" : qUnion([Q0]), "depth" : 1200 * mm});
        }
        {
            var Q0;
            Q0=makeQuery(id+"F13.opExtrude","CAP_FACE",FACE,{"disambiguationData":[OSD([sQuery(id+"F12.wireOp",EDGE,"E19.bottom"),sQuery(id+"F12.wireOp",EDGE,"E19.top"),sQuery(id+"F12.wireOp",EDGE,"E19.left"),sQuery(id+"F12.wireOp",EDGE,"E19.right")])],"isStart":true});
            var sketch = newSketch(context, id + "F46", { "sketchPlane" : qUnion([Q0])});
            skLineSegment(sketch, "E80.bottom", {"start": v(13440, -1150) * mm, "end": v(13470, -1150) * mm});
            skLineSegment(sketch, "E80.top", {"start": v(13440, -1180) * mm, "end": v(13470, -1180) * mm});
            skLineSegment(sketch, "E80.left", {"start": v(13440, -1150) * mm, "end": v(13440, -1180) * mm});
            skLineSegment(sketch, "E80.right", {"start": v(13470, -1150) * mm, "end": v(13470, -1180) * mm});
            skLineSegment(sketch, "E81.bottom", {"start": v(14470, -2420) * mm, "end": v(14500, -2420) * mm});
            skLineSegment(sketch, "E81.top", {"start": v(14470, -2450) * mm, "end": v(14500, -2450) * mm});
            skLineSegment(sketch, "E81.left", {"start": v(14470, -2420) * mm, "end": v(14470, -2450) * mm});
            skLineSegment(sketch, "E81.right", {"start": v(14500, -2420) * mm, "end": v(14500, -2450) * mm});
            skLineSegment(sketch, "E82.bottom", {"start": v(14470, -1150) * mm, "end": v(14500, -1150) * mm});
            skLineSegment(sketch, "E82.top", {"start": v(14470, -1180) * mm, "end": v(14500, -1180) * mm});
            skLineSegment(sketch, "E82.left", {"start": v(14470, -1150) * mm, "end": v(14470, -1180) * mm});
            skLineSegment(sketch, "E82.right", {"start": v(14500, -1150) * mm, "end": v(14500, -1180) * mm});
            skLineSegment(sketch, "E83.bottom", {"start": v(13000, -2420) * mm, "end": v(13030, -2420) * mm});
            skLineSegment(sketch, "E83.top", {"start": v(13000, -2450) * mm, "end": v(13030, -2450) * mm});
            skLineSegment(sketch, "E83.left", {"start": v(13000, -2420) * mm, "end": v(13000, -2450) * mm});
            skLineSegment(sketch, "E83.right", {"start": v(13030, -2420) * mm, "end": v(13030, -2450) * mm});
            skLineSegment(sketch, "E84.bottom", {"start": v(13000, -1940) * mm, "end": v(13030, -1940) * mm});
            skLineSegment(sketch, "E84.top", {"start": v(13000, -1970) * mm, "end": v(13030, -1970) * mm});
            skLineSegment(sketch, "E84.left", {"start": v(13000, -1940) * mm, "end": v(13000, -1970) * mm});
            skLineSegment(sketch, "E84.right", {"start": v(13030, -1940) * mm, "end": v(13030, -1970) * mm});
            skLineSegment(sketch, "E85.bottom", {"start": v(13376.77, -1895) * mm, "end": v(13406.77, -1895) * mm});
            skLineSegment(sketch, "E85.top", {"start": v(13376.77, -1925) * mm, "end": v(13406.77, -1925) * mm});
            skLineSegment(sketch, "E85.left", {"start": v(13376.77, -1895) * mm, "end": v(13376.77, -1925) * mm});
            skLineSegment(sketch, "E85.right", {"start": v(13406.77, -1895) * mm, "end": v(13406.77, -1925) * mm});
            skSolve(sketch);
        }
        {
            var Q0;
            Q0 = qSketchRegion(id + "F46", true);
            extrude(context, id + "F47", {"entities" : qUnion([Q0]), "depth" : 1200 * mm});
        }
        {
            var Q0;
            Q0=qCreatedBy(makeId("Top.planeOp"),FACE);
            var Q1;
            Q1=makeQuery(id+"F43.opExtrude","CAP_VERTEX",VERTEX,{"disambiguationData":[OSD([sQuery(id+"F3.wireOp",EDGE,"E6"),sQuery(id+"F42.wireOp",EDGE,"E68.top"),sQuery(id+"F42.wireOp",EDGE,"E68.left")])],"isStart":false});
            cPlane(context, id + "F48", {"entities" : qUnion([Q0, Q1]), "cplaneType" : CPlaneType.PLANE_POINT, "offset" : 25 * mm, "width" : 150 * mm, "height" : 150 * mm});
        }
        {
            var Q0;
            Q0=qCreatedBy(id+"F48.planeOp",FACE);
            var sketch = newSketch(context, id + "F49", { "sketchPlane" : qUnion([Q0])});
            skLineSegment(sketch, "E86", {"start": v(4015, -1180) * mm, "end": v(4015, -1735) * mm});
            skLineSegment(sketch, "E87", {"start": v(4015, -1735) * mm, "end": v(7015, -1735) * mm});
            skLineSegment(sketch, "E88", {"start": v(7015, -1735) * mm, "end": v(7015, -1935) * mm});
            skLineSegment(sketch, "E89", {"start": v(7015, -1935) * mm, "end": v(9735, -1935) * mm});
            skSolve(sketch);
        }
        {
            var Q0;
            Q0=makeQuery(id+"F43.opExtrude","SWEPT_FACE",FACE,{"disambiguationData":[OSD([sQuery(id+"F42.wireOp",EDGE,"E68.top")])]});
            var sketch = newSketch(context, id + "F50", { "sketchPlane" : qUnion([Q0])});
            skLineSegment(sketch, "E90.bottom", {"start": v(4000, 4700) * mm, "end": v(4030, 4700) * mm});
            skLineSegment(sketch, "E90.top", {"start": v(4000, 4670) * mm, "end": v(4030, 4670) * mm});
            skLineSegment(sketch, "E90.left", {"start": v(4000, 4700) * mm, "end": v(4000, 4670) * mm});
            skLineSegment(sketch, "E90.right", {"start": v(4030, 4700) * mm, "end": v(4030, 4670) * mm});
            skSolve(sketch);
        }
        {
            var Q0;
            Q0=makeQuery(id+"F50.imprint","IMPRINT",FACE,{"disambiguationData":[TD([[makeQuery(id+"F50.imprint","IMPRINT",EDGE,{"derivedFrom":sQuery(id+"F50.wireOp",EDGE,"E90.bottom")}),-1.0]])]});
            var Q1;
            Q1=sQuery(id+"F49.wireOp",EDGE,"E86");
            var Q2;
            Q2=sQuery(id+"F49.wireOp",EDGE,"E87");
            var Q3;
            Q3=sQuery(id+"F49.wireOp",EDGE,"E88");
            var Q4;
            Q4=sQuery(id+"F49.wireOp",EDGE,"E89");
            sweep(context, id + "F51", {"operationType" : NewBodyOperationType.ADD, "profiles" : qUnion([Q0]), "path" : qUnion([Q1, Q2, Q3, Q4])});
        }
        {
            var Q0;
            Q0=qCreatedBy(id+"F48.planeOp",FACE);
            cPlane(context, id + "F52", {"entities" : qUnion([Q0]), "cplaneType" : CPlaneType.OFFSET, "offset" : 350 * mm, "oppositeDirection" : true, "width" : 150 * mm, "height" : 150 * mm});
        }
        {
            var Q0;
            Q0=qCreatedBy(id+"F52.planeOp",FACE);
            var sketch = newSketch(context, id + "F53", { "sketchPlane" : qUnion([Q0])});
            skLineSegment(sketch, "E91.0", {"start": v(4015, -1180) * mm, "end": v(4015, -1735) * mm});
            skLineSegment(sketch, "E92.0", {"start": v(4015, -1735) * mm, "end": v(7015, -1735) * mm});
            skLineSegment(sketch, "E93.0", {"start": v(7015, -1735) * mm, "end": v(7015, -1935) * mm});
            skLineSegment(sketch, "E94.0", {"start": v(7015, -1935) * mm, "end": v(9735, -1935) * mm});
            skSolve(sketch);
        }
        {
            var Q0;
            Q0=makeQuery(id+"F43.opExtrude","SWEPT_FACE",FACE,{"disambiguationData":[OSD([sQuery(id+"F42.wireOp",EDGE,"E68.top")])]});
            var sketch = newSketch(context, id + "F54", { "sketchPlane" : qUnion([Q0])});
            skLineSegment(sketch, "E95.bottom", {"start": v(4000, 4365) * mm, "end": v(4030, 4365) * mm});
            skLineSegment(sketch, "E95.top", {"start": v(4000, 4335) * mm, "end": v(4030, 4335) * mm});
            skLineSegment(sketch, "E95.left", {"start": v(4000, 4365) * mm, "end": v(4000, 4335) * mm});
            skLineSegment(sketch, "E95.right", {"start": v(4030, 4365) * mm, "end": v(4030, 4335) * mm});
            skLineSegment(sketch, "E96", {"start": v(4000, 4365) * mm, "end": v(4030, 4335) * mm, "construction": true});
            skSolve(sketch);
        }
        {
            var Q0;
            Q0 = qSketchRegion(id + "F54", true);
            var Q1;
            Q1=sQuery(id+"F53.wireOp",EDGE,"E91.0");
            var Q2;
            Q2=sQuery(id+"F53.wireOp",EDGE,"E92.0");
            var Q3;
            Q3=sQuery(id+"F53.wireOp",EDGE,"E93.0");
            var Q4;
            Q4=sQuery(id+"F53.wireOp",EDGE,"E94.0");
            sweep(context, id + "F55", {"operationType" : NewBodyOperationType.ADD, "profiles" : qUnion([Q0]), "path" : qUnion([Q1, Q2, Q3, Q4])});
        }
        {
            var Q0;
            Q0=makeQuery(id+"F45.opExtrude","CAP_EDGE",EDGE,{"disambiguationData":[OSD([sQuery(id+"F44.wireOp",EDGE,"E73.left")])],"isStart":false});
            cPoint(context, id + "F56", {"entities" : qUnion([Q0]), "parameter" : 0.5});
        }
        {
            var Q0;
            Q0=makeQuery(id+"F45.opExtrude","SWEPT_FACE",FACE,{"disambiguationData":[OSD([sQuery(id+"F44.wireOp",EDGE,"E73.top")])]});
            var Q1;
            Q1 = qCreatedBy(id + "F56" ,VERTEX);
            cPlane(context, id + "F57", {"entities" : qUnion([Q0, Q1]), "cplaneType" : CPlaneType.PLANE_POINT, "offset" : 25 * mm, "width" : 150 * mm, "height" : 150 * mm});
        }
        {
            var Q0;
            Q0=qCreatedBy(id+"F57.planeOp",FACE);
            var sketch = newSketch(context, id + "F58", { "sketchPlane" : qUnion([Q0])});
            skLineSegment(sketch, "E97", {"start": v(12485, 5785) * mm, "end": v(10515, 5785) * mm});
            skLineSegment(sketch, "E98", {"start": v(10515, 5785) * mm, "end": v(9749.77, 4692.14) * mm});
            skLineSegment(sketch, "E99", {"start": v(12485, 5785) * mm, "end": v(13384.77, 4500) * mm});
            skSolve(sketch);
        }
        {
            var Q0;
            Q0=sQuery(id+"F58.wireOp",VERTEX,"E98.end");
            var Q1;
            Q1=sQuery(id+"F58.wireOp",EDGE,"E98");
            cPlane(context, id + "F59", {"entities" : qUnion([Q0, Q1]), "cplaneType" : CPlaneType.LINE_POINT, "offset" : 25 * mm, "width" : 150 * mm, "height" : 150 * mm});
        }
        {
            var Q0;
            Q0=qCreatedBy(id+"F59.planeOp",FACE);
            var sketch = newSketch(context, id + "F60", { "sketchPlane" : qUnion([Q0])});
            skPoint(sketch, "E100.0", {"position": v(5295.24, 1910) * mm});
            skLineSegment(sketch, "E101.bottom", {"start": v(5280.24, 1895) * mm, "end": v(5310.24, 1895) * mm});
            skLineSegment(sketch, "E101.top", {"start": v(5280.24, 1925) * mm, "end": v(5310.24, 1925) * mm});
            skLineSegment(sketch, "E101.left", {"start": v(5280.24, 1895) * mm, "end": v(5280.24, 1925) * mm});
            skLineSegment(sketch, "E101.right", {"start": v(5310.24, 1895) * mm, "end": v(5310.24, 1925) * mm});
            skSolve(sketch);
        }
        {
            var Q0;
            Q0=makeQuery(id+"F60.imprint","IMPRINT",FACE,{"disambiguationData":[TD([[makeQuery(id+"F60.imprint","IMPRINT",EDGE,{"derivedFrom":sQuery(id+"F60.wireOp",EDGE,"E101.bottom")}),1.0]])]});
            var Q1;
            Q1=sQuery(id+"F58.wireOp",EDGE,"E98");
            var Q2;
            Q2=sQuery(id+"F58.wireOp",EDGE,"E97");
            var Q3;
            Q3=sQuery(id+"F58.wireOp",EDGE,"E99");
            sweep(context, id + "F61", {"profiles" : qUnion([Q0]), "path" : qUnion([Q1, Q2, Q3])});
        }
        {
            var Q0;
            Q0=qCreatedBy(id+"F57.planeOp",FACE);
            var sketch = newSketch(context, id + "F62", { "sketchPlane" : qUnion([Q0])});
            skLineSegment(sketch, "E102", {"start": v(12485, 5435) * mm, "end": v(10515, 5435) * mm});
            skLineSegment(sketch, "E103", {"start": v(10515, 5435) * mm, "end": v(9749.77, 4342.14) * mm});
            skLineSegment(sketch, "E104", {"start": v(12485, 5435) * mm, "end": v(13384.77, 4150) * mm});
            skSolve(sketch);
        }
        {
            var Q0;
            Q0=sQuery(id+"F62.wireOp",VERTEX,"E103.end");
            var Q1;
            Q1=sQuery(id+"F62.wireOp",EDGE,"E103");
            cPlane(context, id + "F63", {"entities" : qUnion([Q0, Q1]), "cplaneType" : CPlaneType.LINE_POINT, "offset" : 25 * mm, "width" : 150 * mm, "height" : 150 * mm});
        }
        {
            var Q0;
            Q0=qCreatedBy(id+"F63.planeOp",FACE);
            var sketch = newSketch(context, id + "F64", { "sketchPlane" : qUnion([Q0])});
            skPoint(sketch, "E105.0", {"position": v(5496, 1910) * mm});
            skLineSegment(sketch, "E106.bottom", {"start": v(5511, 1895) * mm, "end": v(5481, 1895) * mm});
            skLineSegment(sketch, "E106.top", {"start": v(5511, 1925) * mm, "end": v(5481, 1925) * mm});
            skLineSegment(sketch, "E106.left", {"start": v(5511, 1895) * mm, "end": v(5511, 1925) * mm});
            skLineSegment(sketch, "E106.right", {"start": v(5481, 1895) * mm, "end": v(5481, 1925) * mm});
            skSolve(sketch);
        }
        {
            var Q0;
            Q0 = qSketchRegion(id + "F64", true);
            var Q1;
            Q1=sQuery(id+"F62.wireOp",EDGE,"E103");
            var Q2;
            Q2=sQuery(id+"F62.wireOp",EDGE,"E102");
            var Q3;
            Q3=sQuery(id+"F62.wireOp",EDGE,"E104");
            sweep(context, id + "F65", {"profiles" : qUnion([Q0]), "path" : qUnion([Q1, Q2, Q3])});
        }
        {
            var Q0;
            Q0=makeQuery(id+"F47.opExtrude","CAP_FACE",FACE,{"disambiguationData":[OSD([sQuery(id+"F46.wireOp",EDGE,"E84.bottom"),sQuery(id+"F46.wireOp",EDGE,"E84.top"),sQuery(id+"F46.wireOp",EDGE,"E84.left"),sQuery(id+"F46.wireOp",EDGE,"E84.right")])],"isStart":false});
            cPlane(context, id + "F66", {"entities" : qUnion([Q0]), "cplaneType" : CPlaneType.OFFSET, "offset" : 15 * mm, "oppositeDirection" : true, "width" : 150 * mm, "height" : 150 * mm});
        }
        {
            var Q0;
            Q0=qCreatedBy(id+"F66.planeOp",FACE);
            var sketch = newSketch(context, id + "F67", { "sketchPlane" : qUnion([Q0])});
            skLineSegment(sketch, "E107", {"start": v(13015, -1955) * mm, "end": v(13015, -2435) * mm});
            skLineSegment(sketch, "E108", {"start": v(13015, -2435) * mm, "end": v(14485, -2435) * mm});
            skLineSegment(sketch, "E109", {"start": v(14485, -2435) * mm, "end": v(14485, -1165) * mm});
            skLineSegment(sketch, "E110", {"start": v(14485, -1165) * mm, "end": v(13455, -1165) * mm});
            skSolve(sketch);
        }
        {
            var Q0;
            Q0=makeQuery(id+"F47.opExtrude","SWEPT_FACE",FACE,{"disambiguationData":[OSD([sQuery(id+"F46.wireOp",EDGE,"E80.right")])]});
            var sketch = newSketch(context, id + "F68", { "sketchPlane" : qUnion([Q0])});
            skLineSegment(sketch, "E111.bottom", {"start": v(-1180, 4500) * mm, "end": v(-1150, 4500) * mm});
            skLineSegment(sketch, "E111.top", {"start": v(-1180, 4470) * mm, "end": v(-1150, 4470) * mm});
            skLineSegment(sketch, "E111.left", {"start": v(-1180, 4500) * mm, "end": v(-1180, 4470) * mm});
            skLineSegment(sketch, "E111.right", {"start": v(-1150, 4500) * mm, "end": v(-1150, 4470) * mm});
            skSolve(sketch);
        }
        {
            var Q0;
            Q0=makeQuery(id+"F68.imprint","IMPRINT",FACE,{"disambiguationData":[TD([[makeQuery(id+"F68.imprint","IMPRINT",EDGE,{"derivedFrom":sQuery(id+"F68.wireOp",EDGE,"E111.bottom")}),1.0]])]});
            var Q1;
            Q1=sQuery(id+"F67.wireOp",EDGE,"E110");
            var Q2;
            Q2=sQuery(id+"F67.wireOp",EDGE,"E109");
            var Q3;
            Q3=sQuery(id+"F67.wireOp",EDGE,"E108");
            var Q4;
            Q4=sQuery(id+"F67.wireOp",EDGE,"E107");
            sweep(context, id + "F69", {"profiles" : qUnion([Q0]), "path" : qUnion([Q1, Q2, Q3, Q4])});
        }
        {
            var Q0;
            Q0=qCreatedBy(id+"F66.planeOp",FACE);
            cPlane(context, id + "F70", {"entities" : qUnion([Q0]), "cplaneType" : CPlaneType.OFFSET, "offset" : 350 * mm, "oppositeDirection" : true, "width" : 150 * mm, "height" : 150 * mm});
        }
        {
            var Q0;
            Q0=qCreatedBy(id+"F70.planeOp",FACE);
            var sketch = newSketch(context, id + "F71", { "sketchPlane" : qUnion([Q0])});
            skLineSegment(sketch, "E112.0", {"start": v(13015, -1955) * mm, "end": v(13015, -2435) * mm});
            skLineSegment(sketch, "E113.0", {"start": v(13015, -2435) * mm, "end": v(14485, -2435) * mm});
            skLineSegment(sketch, "E114.0", {"start": v(14485, -2435) * mm, "end": v(14485, -1165) * mm});
            skLineSegment(sketch, "E115.0", {"start": v(14485, -1165) * mm, "end": v(13455, -1165) * mm});
            skSolve(sketch);
        }
        {
            var Q0;
            Q0=makeQuery(id+"F47.opExtrude","SWEPT_FACE",FACE,{"disambiguationData":[OSD([sQuery(id+"F46.wireOp",EDGE,"E80.right")])]});
            var sketch = newSketch(context, id + "F72", { "sketchPlane" : qUnion([Q0])});
            skPoint(sketch, "E116.0", {"position": v(-1165, 4135) * mm});
            skLineSegment(sketch, "E117.bottom", {"start": v(-1150, 4150) * mm, "end": v(-1180, 4150) * mm});
            skLineSegment(sketch, "E117.top", {"start": v(-1150, 4120) * mm, "end": v(-1180, 4120) * mm});
            skLineSegment(sketch, "E117.left", {"start": v(-1150, 4150) * mm, "end": v(-1150, 4120) * mm});
            skLineSegment(sketch, "E117.right", {"start": v(-1180, 4150) * mm, "end": v(-1180, 4120) * mm});
            skSolve(sketch);
        }
        {
            var Q0;
            Q0=makeQuery(id+"F72.imprint","IMPRINT",FACE,{"disambiguationData":[TD([[makeQuery(id+"F72.imprint","IMPRINT",EDGE,{"derivedFrom":sQuery(id+"F72.wireOp",EDGE,"E117.bottom")}),1.0]])]});
            var Q1;
            Q1=sQuery(id+"F71.wireOp",EDGE,"E115.0");
            var Q2;
            Q2=sQuery(id+"F71.wireOp",EDGE,"E114.0");
            var Q3;
            Q3=sQuery(id+"F71.wireOp",EDGE,"E113.0");
            var Q4;
            Q4=sQuery(id+"F71.wireOp",EDGE,"E112.0");
            sweep(context, id + "F73", {"profiles" : qUnion([Q0]), "path" : qUnion([Q1, Q2, Q3, Q4])});
        }
        {
            var Q0;
            Q0=makeQuery(id+"F45.opExtrude","CAP_EDGE",EDGE,{"disambiguationData":[OSD([sQuery(id+"F44.wireOp",EDGE,"E79.bottom")])],"isStart":false});
            cPoint(context, id + "F74", {"entities" : qUnion([Q0]), "parameter" : 0.5});
        }
        {
            var Q0;
            Q0=makeQuery(id+"F45.opExtrude","SWEPT_FACE",FACE,{"disambiguationData":[OSD([sQuery(id+"F44.wireOp",EDGE,"E79.left")])]});
            var Q1;
            Q1 = qCreatedBy(id + "F74" ,VERTEX);
            cPlane(context, id + "F75", {"entities" : qUnion([Q0, Q1]), "cplaneType" : CPlaneType.PLANE_POINT, "offset" : 25 * mm, "width" : 150 * mm, "height" : 150 * mm});
        }
        {
            var Q0;
            Q0=qCreatedBy(id+"F75.planeOp",FACE);
            var sketch = newSketch(context, id + "F76", { "sketchPlane" : qUnion([Q0])});
            skLineSegment(sketch, "E118", {"start": v(1160, 5785) * mm, "end": v(140, 5785) * mm});
            skLineSegment(sketch, "E119", {"start": v(140, 5785) * mm, "end": v(-521, 4840.99) * mm});
            skLineSegment(sketch, "E120", {"start": v(-521, 4840.99) * mm, "end": v(-521, 3672.4) * mm});
            skSolve(sketch);
        }
        {
            var Q0;
            Q0=makeQuery(id+"F45.opExtrude","SWEPT_FACE",FACE,{"disambiguationData":[OSD([sQuery(id+"F44.wireOp",EDGE,"E79.bottom")])]});
            var sketch = newSketch(context, id + "F77", { "sketchPlane" : qUnion([Q0])});
            skLineSegment(sketch, "E121.bottom", {"start": v(-10530, 5800) * mm, "end": v(-10500, 5800) * mm});
            skLineSegment(sketch, "E121.top", {"start": v(-10530, 5770) * mm, "end": v(-10500, 5770) * mm});
            skLineSegment(sketch, "E121.left", {"start": v(-10530, 5800) * mm, "end": v(-10530, 5770) * mm});
            skLineSegment(sketch, "E121.right", {"start": v(-10500, 5800) * mm, "end": v(-10500, 5770) * mm});
            skSolve(sketch);
        }
        {
            var Q0;
            Q0=makeQuery(id+"F77.imprint","IMPRINT",FACE,{"disambiguationData":[TD([[makeQuery(id+"F77.imprint","IMPRINT",EDGE,{"derivedFrom":sQuery(id+"F77.wireOp",EDGE,"E121.bottom")}),1.0]])]});
            var Q1;
            Q1=sQuery(id+"F76.wireOp",EDGE,"E118");
            var Q2;
            Q2=sQuery(id+"F76.wireOp",EDGE,"E119");
            var Q3;
            Q3=sQuery(id+"F76.wireOp",EDGE,"E120");
            sweep(context, id + "F78", {"profiles" : qUnion([Q0]), "path" : qUnion([Q1, Q2, Q3])});
        }
        {
            var Q0;
            Q0=qCreatedBy(id+"F75.planeOp",FACE);
            var sketch = newSketch(context, id + "F79", { "sketchPlane" : qUnion([Q0])});
            skLineSegment(sketch, "E122", {"start": v(1160, 5420) * mm, "end": v(140, 5420) * mm});
            skLineSegment(sketch, "E123", {"start": v(140, 5420) * mm, "end": v(-521, 4475.99) * mm});
            skSolve(sketch);
        }
        {
            var Q0;
            Q0=makeQuery(id+"F45.opExtrude","SWEPT_FACE",FACE,{"disambiguationData":[OSD([sQuery(id+"F44.wireOp",EDGE,"E79.bottom")])]});
            var sketch = newSketch(context, id + "F80", { "sketchPlane" : qUnion([Q0])});
            skPoint(sketch, "E124.0", {"position": v(-10515, 5420) * mm});
            skLineSegment(sketch, "E125.bottom", {"start": v(-10500, 5405) * mm, "end": v(-10530, 5405) * mm});
            skLineSegment(sketch, "E125.top", {"start": v(-10500, 5435) * mm, "end": v(-10530, 5435) * mm});
            skLineSegment(sketch, "E125.left", {"start": v(-10500, 5405) * mm, "end": v(-10500, 5435) * mm});
            skLineSegment(sketch, "E125.right", {"start": v(-10530, 5405) * mm, "end": v(-10530, 5435) * mm});
            skSolve(sketch);
        }
        {
            var Q0;
            Q0=makeQuery(id+"F80.imprint","IMPRINT",FACE,{"disambiguationData":[TD([[makeQuery(id+"F80.imprint","IMPRINT",EDGE,{"derivedFrom":sQuery(id+"F80.wireOp",EDGE,"E125.bottom")}),-1.0]])]});
            var Q1;
            Q1=sQuery(id+"F79.wireOp",EDGE,"E122");
            var Q2;
            Q2=sQuery(id+"F79.wireOp",EDGE,"E123");
            sweep(context, id + "F81", {"profiles" : qUnion([Q0]), "path" : qUnion([Q1, Q2])});
        }
        {
            var Q0;
            Q0=makeQuery(id+"F78.opSweep","SWEPT_BODY",BODY,{"disambiguationData":[OSD([sQuery(id+"F76.wireOp",EDGE,"E120"),sQuery(id+"F77.wireOp",EDGE,"E121.bottom"),sQuery(id+"F77.wireOp",EDGE,"E121.top"),sQuery(id+"F77.wireOp",EDGE,"E121.left"),sQuery(id+"F77.wireOp",EDGE,"E121.right")])]});
            var Q1;
            Q1=makeQuery(id+"F81.opSweep","SWEPT_BODY",BODY,{"disambiguationData":[OSD([sQuery(id+"F79.wireOp",EDGE,"E123"),sQuery(id+"F80.wireOp",EDGE,"E125.bottom"),sQuery(id+"F80.wireOp",EDGE,"E125.top"),sQuery(id+"F80.wireOp",EDGE,"E125.left"),sQuery(id+"F80.wireOp",EDGE,"E125.right")])]});
            var Q2;
            Q2=qCreatedBy(id+"F25.planeOp",FACE);
            mirror(context, id + "F82", {"entities" : qUnion([Q0, Q1]), "mirrorPlane" : qUnion([Q2])});
        }
        {
            var Q0;
            Q0=makeQuery(id+"F45.opExtrude","CAP_EDGE",EDGE,{"disambiguationData":[OSD([sQuery(id+"F44.wireOp",EDGE,"E75.right")])],"isStart":false});
            cPoint(context, id + "F83", {"entities" : qUnion([Q0]), "parameter" : 0.5});
        }
        {
            var Q0;
            Q0=makeQuery(id+"F45.opExtrude","SWEPT_FACE",FACE,{"disambiguationData":[OSD([sQuery(id+"F44.wireOp",EDGE,"E75.bottom")])]});
            var Q1;
            Q1 = qCreatedBy(id + "F83" ,VERTEX);
            cPlane(context, id + "F84", {"entities" : qUnion([Q0, Q1]), "cplaneType" : CPlaneType.PLANE_POINT, "offset" : 25 * mm, "width" : 150 * mm, "height" : 150 * mm});
        }
        {
            var Q0;
            Q0=qCreatedBy(id+"F84.planeOp",FACE);
            var sketch = newSketch(context, id + "F85", { "sketchPlane" : qUnion([Q0])});
            skLineSegment(sketch, "E126", {"start": v(-11385, 5785) * mm, "end": v(-12485, 5785) * mm});
            skLineSegment(sketch, "E127", {"start": v(-12485, 5785) * mm, "end": v(-13392.54, 4488.9) * mm});
            skSolve(sketch);
        }
        {
            var Q0;
            Q0=makeQuery(id+"F45.opExtrude","SWEPT_FACE",FACE,{"disambiguationData":[OSD([sQuery(id+"F44.wireOp",EDGE,"E75.right")])]});
            var sketch = newSketch(context, id + "F86", { "sketchPlane" : qUnion([Q0])});
            skLineSegment(sketch, "E128.bottom", {"start": v(-1205, 5800) * mm, "end": v(-1175, 5800) * mm});
            skLineSegment(sketch, "E128.top", {"start": v(-1205, 5770) * mm, "end": v(-1175, 5770) * mm});
            skLineSegment(sketch, "E128.left", {"start": v(-1205, 5800) * mm, "end": v(-1205, 5770) * mm});
            skLineSegment(sketch, "E128.right", {"start": v(-1175, 5800) * mm, "end": v(-1175, 5770) * mm});
            skSolve(sketch);
        }
        {
            var Q0;
            Q0=makeQuery(id+"F86.imprint","IMPRINT",FACE,{"disambiguationData":[TD([[makeQuery(id+"F86.imprint","IMPRINT",EDGE,{"derivedFrom":sQuery(id+"F86.wireOp",EDGE,"E128.bottom")}),1.0]])]});
            var Q1;
            Q1=sQuery(id+"F85.wireOp",EDGE,"E126");
            var Q2;
            Q2=sQuery(id+"F85.wireOp",EDGE,"E127");
            sweep(context, id + "F87", {"profiles" : qUnion([Q0]), "path" : qUnion([Q1, Q2])});
        }
        {
            var Q0;
            Q0=qCreatedBy(id+"F84.planeOp",FACE);
            var sketch = newSketch(context, id + "F88", { "sketchPlane" : qUnion([Q0])});
            skLineSegment(sketch, "E129", {"start": v(-11385, 5435) * mm, "end": v(-12485, 5435) * mm});
            skLineSegment(sketch, "E130", {"start": v(-12485, 5435) * mm, "end": v(-13384.77, 4150) * mm});
            skSolve(sketch);
        }
        {
            var Q0;
            Q0=makeQuery(id+"F45.opExtrude","SWEPT_FACE",FACE,{"disambiguationData":[OSD([sQuery(id+"F44.wireOp",EDGE,"E75.right")])]});
            var sketch = newSketch(context, id + "F89", { "sketchPlane" : qUnion([Q0])});
            skPoint(sketch, "E131.0", {"position": v(-1190, 5435) * mm});
            skLineSegment(sketch, "E132.bottom", {"start": v(-1205, 5450) * mm, "end": v(-1175, 5450) * mm});
            skLineSegment(sketch, "E132.top", {"start": v(-1205, 5420) * mm, "end": v(-1175, 5420) * mm});
            skLineSegment(sketch, "E132.left", {"start": v(-1205, 5450) * mm, "end": v(-1205, 5420) * mm});
            skLineSegment(sketch, "E132.right", {"start": v(-1175, 5450) * mm, "end": v(-1175, 5420) * mm});
            skSolve(sketch);
        }
        {
            var Q0;
            Q0=makeQuery(id+"F89.imprint","IMPRINT",FACE,{"disambiguationData":[TD([[makeQuery(id+"F89.imprint","IMPRINT",EDGE,{"derivedFrom":sQuery(id+"F89.wireOp",EDGE,"E132.bottom")}),-1.0]])]});
            var Q1;
            Q1=sQuery(id+"F88.wireOp",EDGE,"E129");
            var Q2;
            Q2=sQuery(id+"F88.wireOp",EDGE,"E130");
            sweep(context, id + "F90", {"profiles" : qUnion([Q0]), "path" : qUnion([Q1, Q2])});
        }
    });
